# Revit family: Lollygagger No9 Otto man
name_source: partatom
category: Furniture
revit_build: Autodesk Revit 2016 (Build: 20150220_1215(x64)
units: mm (PartAtom-declared; Revit-internal decimal feet)

## family parameters
Always vertical = Yes
Cut with Voids When Loaded = No
OmniClass Number = 23.40.20.00
OmniClass Title = General Furniture and Specialties
Room Calculation Point = No
Shared = No
Work Plane-Based = No

## types (10) — shared parameters
Length = 17 1/2"
Manufacturer = Loll
Thick = 1"
Type Image = No9 ottoman.jpg
URL = https://lolldesigns.com
Width = 19"

## per-type parameters (varying)
| type | Height |
| Loll-Black | 9 29/32" |
| Loll-Sunset | 28 23/32" |
| Loll-Chocolate | 28 23/32" |
| Loll-Sky | 28 23/32" |
| Loll-Apple | 28 23/32" |
| Loll-Leaf | 28 23/32" |
| Loll-Charcoal | 28 23/32" |
| Loll-Navy Blue | 9 29/32" |
| Loll-White | 28 23/32" |
| Loll-Driftwood | 28 23/32" |

note: column(s) folded — value = type name in every type: Finish Material

## geometry (parser evidence)
native form markers: Sweep x3
no freeform markers — native parametric forms only
